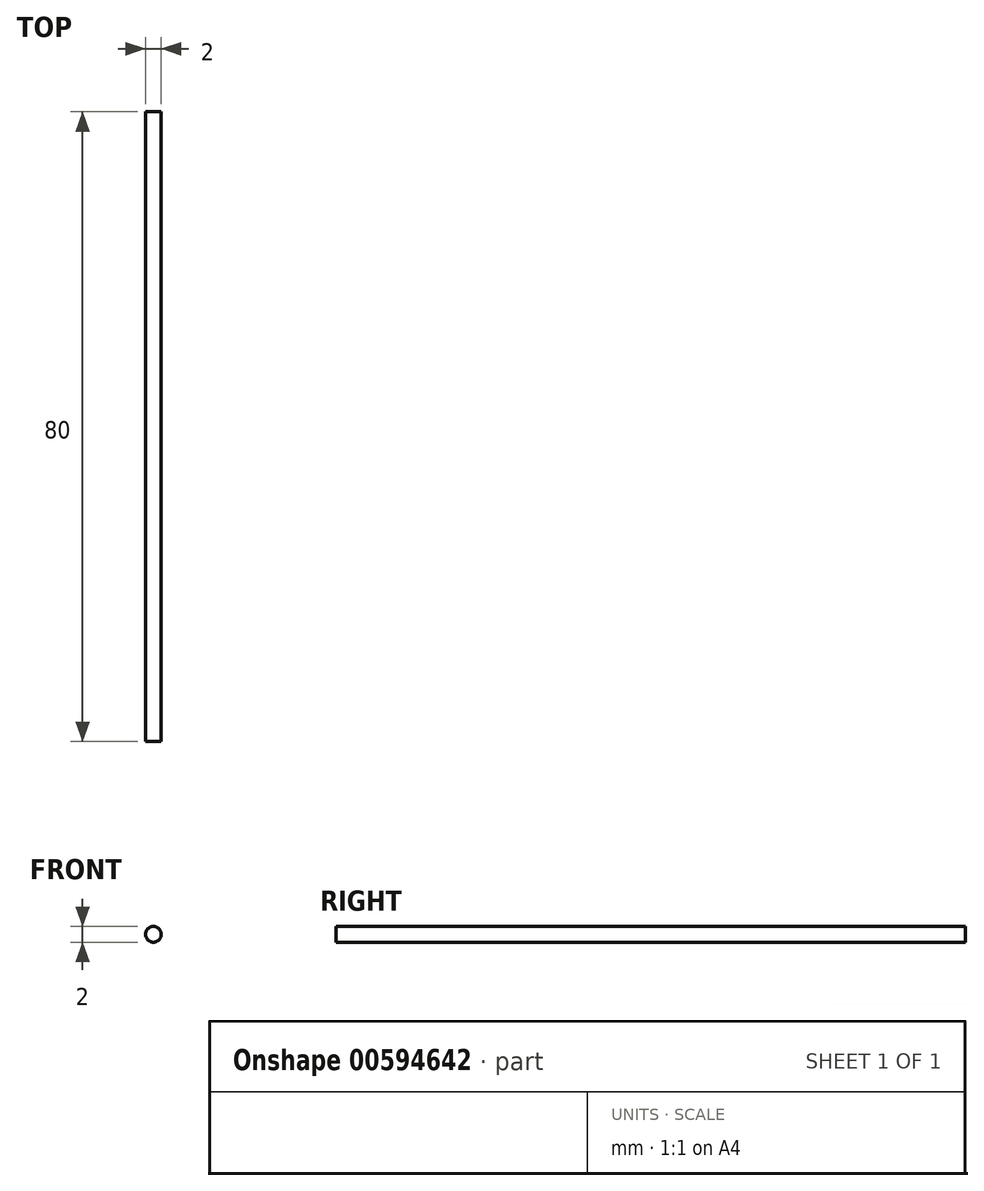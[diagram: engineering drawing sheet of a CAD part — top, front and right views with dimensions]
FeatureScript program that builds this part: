
annotation { "Feature Type Name" : "Feature", "Feature Type Description" : "" }
export const myFeature = defineFeature(function(context is Context, id is Id, definition is map)
    precondition{}
    {
        {
            var Q0;
            Q0=qCreatedBy(makeId("Front.planeOp"),FACE);
            var sketch = newSketch(context, id + "F0", { "sketchPlane" : qUnion([Q0])});
            skCircle(sketch, "E0", {"center": v(0, 0) * mm, "radius": 1 * mm});
            skSolve(sketch);
        }
        {
            var Q0;
            Q0 = qSketchRegion(id + "F0", true);
            extrude(context, id + "F1", {"entities" : qUnion([Q0]), "depth" : 80 * mm, "offsetDistance" : 25.4 * mm});
        }
    });
